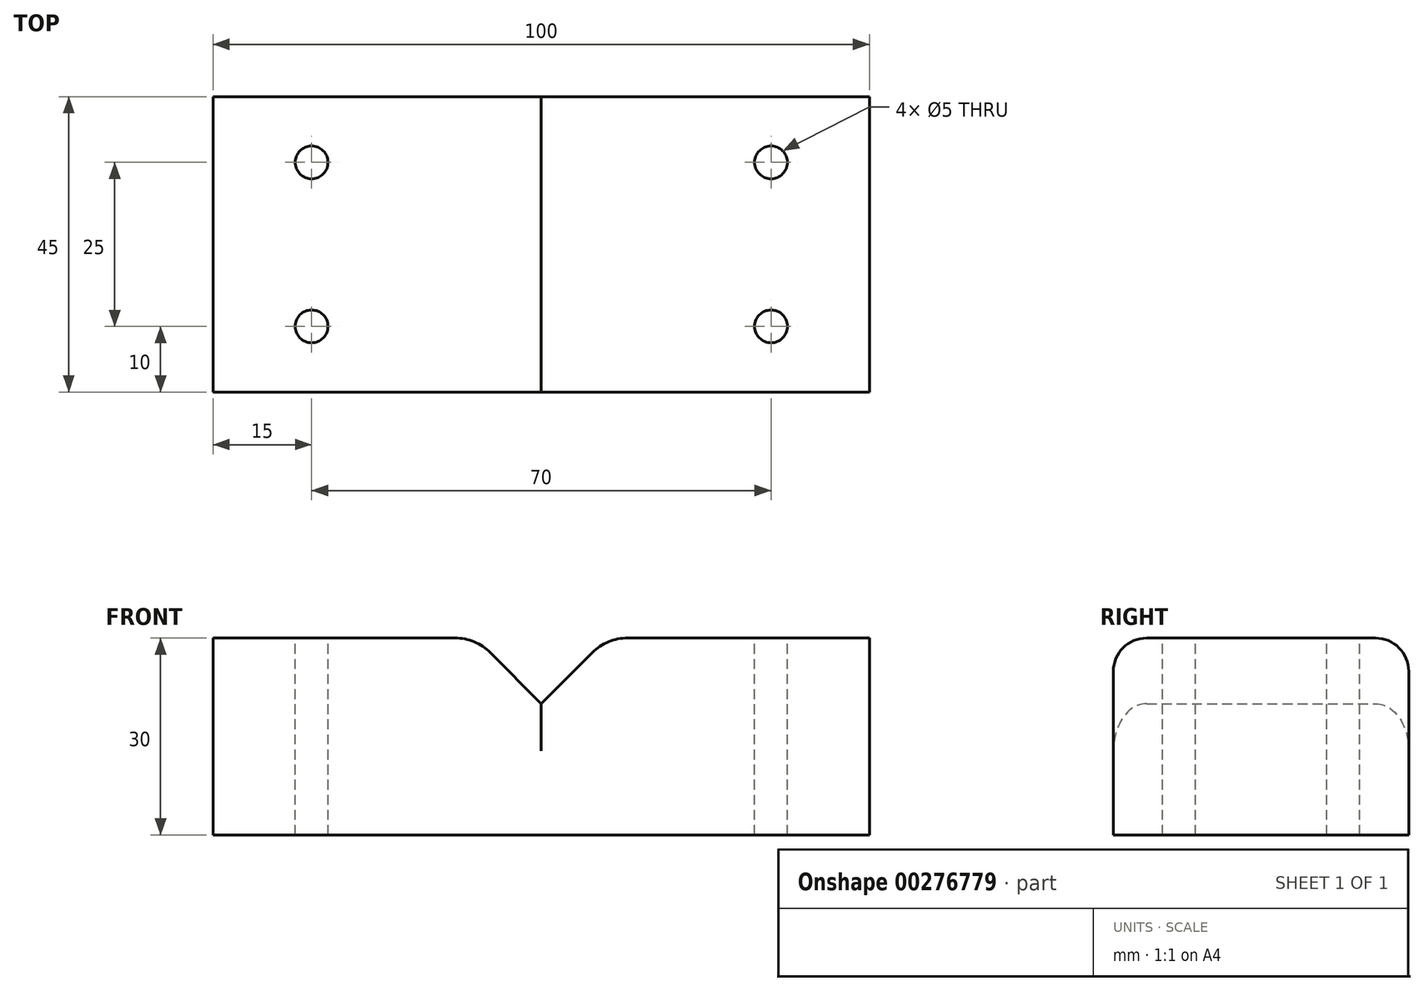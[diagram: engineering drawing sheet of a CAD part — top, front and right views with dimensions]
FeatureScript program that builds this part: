
annotation { "Feature Type Name" : "Feature", "Feature Type Description" : "" }
export const myFeature = defineFeature(function(context is Context, id is Id, definition is map)
    precondition{}
    {
        {
            var Q0;
            Q0=qCreatedBy(makeId("Front.planeOp"),FACE);
            var sketch = newSketch(context, id + "F0", { "sketchPlane" : qUnion([Q0])});
            skPoint(sketch, "E0.middle", {"position": v(0, 0) * mm});
            skLineSegment(sketch, "E1", {"start": v(20, 20) * mm, "end": v(50, 20) * mm});
            skLineSegment(sketch, "E2", {"start": v(50, 20) * mm, "end": v(50, 0) * mm});
            skLineSegment(sketch, "E3", {"start": v(-20, 20) * mm, "end": v(-50, 20) * mm});
            skLineSegment(sketch, "E4", {"start": v(-50, 20) * mm, "end": v(-50, 0) * mm});
            skLineSegment(sketch, "E5", {"start": v(-50, 0) * mm, "end": v(-50, -10) * mm});
            skLineSegment(sketch, "E6", {"start": v(-50, -10) * mm, "end": v(50, -10) * mm});
            skLineSegment(sketch, "E7", {"start": v(50, -10) * mm, "end": v(50, 0) * mm});
            skLineSegment(sketch, "E8", {"start": v(-20, 20) * mm, "end": v(-10, 20) * mm});
            skLineSegment(sketch, "E9", {"start": v(20, 20) * mm, "end": v(10, 20) * mm});
            skLineSegment(sketch, "E10", {"start": v(-10, 20) * mm, "end": v(0, 10) * mm});
            skLineSegment(sketch, "E11", {"start": v(0, 10) * mm, "end": v(10, 20) * mm});
            skSolve(sketch);
        }
        {
            var Q0;
            Q0 = qSketchRegion(id + "F0", true);
            extrude(context, id + "F1", {"entities" : qUnion([Q0]), "depth" : 45 * mm});
        }
        {
            var Q0;
            Q0=makeQuery(id+"F1.opExtrude","SWEPT_FACE",FACE,{"disambiguationData":[OSD([sQuery(id+"F0.wireOp",EDGE,"E1")])]});
            var sketch = newSketch(context, id + "F2", { "sketchPlane" : qUnion([Q0])});
            skCircle(sketch, "E12", {"center": v(35, -35) * mm, "radius": 2 * mm});
            skSolve(sketch);
        }
        {
            var Q0;
            Q0=sQuery(id+"F2.wireOp",VERTEX,"E12.center");
            var Q1;
            Q1=makeQuery(id+"F1.opExtrude","SWEPT_BODY",BODY,{"disambiguationData":[OSD([sQuery(id+"F0.wireOp",EDGE,"76PpERGf-RPlK-5DYp-Uilo-4EMAaiWrKBhD"),sQuery(id+"F0.wireOp",EDGE,"PzodHsil-XRGJ-AnxR-qKlP-lsXBW81SyEPC"),sQuery(id+"F0.wireOp",EDGE,"E1"),sQuery(id+"F0.wireOp",EDGE,"E2"),sQuery(id+"F0.wireOp",EDGE,"E3"),sQuery(id+"F0.wireOp",EDGE,"E4"),sQuery(id+"F0.wireOp",EDGE,"E5"),sQuery(id+"F0.wireOp",EDGE,"E6"),sQuery(id+"F0.wireOp",EDGE,"E7")])]});
            hole(context, id + "F3", {"style" : HoleStyle.SIMPLE, "endStyle" : HoleEndStyle.THROUGH, "holeDiameter" : 5 * mm, "tappedDepth" : 12.7 * mm, "tapClearance" : 3, "locations" : qUnion([Q0]), "scope" : qUnion([Q1])});
        }
        {
            var Q0;
            Q0=makeQuery(id+"F1.opExtrude","SWEPT_FACE",FACE,{"disambiguationData":[OSD([sQuery(id+"F0.wireOp",EDGE,"E1")])]});
            var sketch = newSketch(context, id + "F4", { "sketchPlane" : qUnion([Q0])});
            skCircle(sketch, "E13", {"center": v(35, -10) * mm, "radius": 2 * mm});
            skSolve(sketch);
        }
        {
            var Q0;
            Q0=sQuery(id+"F4.wireOp",VERTEX,"E13.center");
            var Q1;
            Q1=makeQuery(id+"F1.opExtrude","SWEPT_BODY",BODY,{"disambiguationData":[OSD([sQuery(id+"F0.wireOp",EDGE,"76PpERGf-RPlK-5DYp-Uilo-4EMAaiWrKBhD"),sQuery(id+"F0.wireOp",EDGE,"PzodHsil-XRGJ-AnxR-qKlP-lsXBW81SyEPC"),sQuery(id+"F0.wireOp",EDGE,"E1"),sQuery(id+"F0.wireOp",EDGE,"E2"),sQuery(id+"F0.wireOp",EDGE,"E3"),sQuery(id+"F0.wireOp",EDGE,"E4"),sQuery(id+"F0.wireOp",EDGE,"E5"),sQuery(id+"F0.wireOp",EDGE,"E6"),sQuery(id+"F0.wireOp",EDGE,"E7")])]});
            hole(context, id + "F5", {"style" : HoleStyle.SIMPLE, "endStyle" : HoleEndStyle.THROUGH, "holeDiameter" : 5 * mm, "tappedDepth" : 12.7 * mm, "tapClearance" : 3, "locations" : qUnion([Q0]), "scope" : qUnion([Q1])});
        }
        {
            var Q0;
            Q0=makeQuery(id+"F1.opExtrude","SWEPT_FACE",FACE,{"disambiguationData":[OSD([sQuery(id+"F0.wireOp",EDGE,"E3")])]});
            var sketch = newSketch(context, id + "F6", { "sketchPlane" : qUnion([Q0])});
            skCircle(sketch, "E14", {"center": v(-35, -10) * mm, "radius": 2 * mm});
            skSolve(sketch);
        }
        {
            var Q0;
            Q0=sQuery(id+"F6.wireOp",VERTEX,"E14.center");
            var Q1;
            Q1=makeQuery(id+"F1.opExtrude","SWEPT_BODY",BODY,{"disambiguationData":[OSD([sQuery(id+"F0.wireOp",EDGE,"76PpERGf-RPlK-5DYp-Uilo-4EMAaiWrKBhD"),sQuery(id+"F0.wireOp",EDGE,"PzodHsil-XRGJ-AnxR-qKlP-lsXBW81SyEPC"),sQuery(id+"F0.wireOp",EDGE,"E1"),sQuery(id+"F0.wireOp",EDGE,"E2"),sQuery(id+"F0.wireOp",EDGE,"E3"),sQuery(id+"F0.wireOp",EDGE,"E4"),sQuery(id+"F0.wireOp",EDGE,"E5"),sQuery(id+"F0.wireOp",EDGE,"E6"),sQuery(id+"F0.wireOp",EDGE,"E7")])]});
            hole(context, id + "F7", {"style" : HoleStyle.SIMPLE, "endStyle" : HoleEndStyle.THROUGH, "holeDiameter" : 5 * mm, "tappedDepth" : 12.7 * mm, "tapClearance" : 3, "locations" : qUnion([Q0]), "scope" : qUnion([Q1])});
        }
        {
            var Q0;
            Q0=makeQuery(id+"F1.opExtrude","SWEPT_FACE",FACE,{"disambiguationData":[OSD([sQuery(id+"F0.wireOp",EDGE,"E3")])]});
            var sketch = newSketch(context, id + "F8", { "sketchPlane" : qUnion([Q0])});
            skCircle(sketch, "E15", {"center": v(-35, -35) * mm, "radius": 2 * mm});
            skSolve(sketch);
        }
        {
            var Q0;
            Q0=sQuery(id+"F8.wireOp",VERTEX,"E15.center");
            var Q1;
            Q1=makeQuery(id+"F1.opExtrude","SWEPT_BODY",BODY,{"disambiguationData":[OSD([sQuery(id+"F0.wireOp",EDGE,"76PpERGf-RPlK-5DYp-Uilo-4EMAaiWrKBhD"),sQuery(id+"F0.wireOp",EDGE,"PzodHsil-XRGJ-AnxR-qKlP-lsXBW81SyEPC"),sQuery(id+"F0.wireOp",EDGE,"E1"),sQuery(id+"F0.wireOp",EDGE,"E2"),sQuery(id+"F0.wireOp",EDGE,"E3"),sQuery(id+"F0.wireOp",EDGE,"E4"),sQuery(id+"F0.wireOp",EDGE,"E5"),sQuery(id+"F0.wireOp",EDGE,"E6"),sQuery(id+"F0.wireOp",EDGE,"E7")])]});
            hole(context, id + "F9", {"style" : HoleStyle.SIMPLE, "endStyle" : HoleEndStyle.THROUGH, "holeDiameter" : 5 * mm, "tappedDepth" : 12.7 * mm, "tapClearance" : 3, "locations" : qUnion([Q0]), "scope" : qUnion([Q1])});
        }
        {
            var Q0;
            Q0=makeQuery(id+"F1.opExtrude","SWEPT_EDGE",EDGE,{"disambiguationData":[OSD([sQuery(id+"F0.wireOp",EDGE,"E9"),sQuery(id+"F0.wireOp",EDGE,"E11")])]});
            var Q1;
            Q1=makeQuery(id+"F1.opExtrude","SWEPT_EDGE",EDGE,{"disambiguationData":[OSD([sQuery(id+"F0.wireOp",EDGE,"E8"),sQuery(id+"F0.wireOp",EDGE,"E10")])]});
            fillet(context, id + "F10", {"entities" : qUnion([Q0, Q1]), "radius" : 7.62 * mm, "tangentPropagation" : true, "allowEdgeOverflow" : false});
        }
        {
            var Q0;
            Q0=makeQuery(id+"F1.opExtrude","CAP_EDGE",EDGE,{"disambiguationData":[OSD([sQuery(id+"F0.wireOp",EDGE,"E3"),sQuery(id+"F0.wireOp",EDGE,"E8")])],"isStart":false});
            var Q1;
            Q1=makeQuery(id+"F1.opExtrude","CAP_EDGE",EDGE,{"disambiguationData":[OSD([sQuery(id+"F0.wireOp",EDGE,"E1"),sQuery(id+"F0.wireOp",EDGE,"E9")])],"isStart":false});
            var Q2;
            Q2=makeQuery(id+"F1.opExtrude","CAP_EDGE",EDGE,{"disambiguationData":[OSD([sQuery(id+"F0.wireOp",EDGE,"E1"),sQuery(id+"F0.wireOp",EDGE,"E9")])],"isStart":true});
            var Q3;
            Q3=makeQuery(id+"F1.opExtrude","CAP_EDGE",EDGE,{"disambiguationData":[OSD([sQuery(id+"F0.wireOp",EDGE,"E3"),sQuery(id+"F0.wireOp",EDGE,"E8")])],"isStart":true});
            fillet(context, id + "F11", {"entities" : qUnion([Q0, Q1, Q2, Q3]), "radius" : 5.08 * mm, "tangentPropagation" : true, "allowEdgeOverflow" : false});
        }
    });
